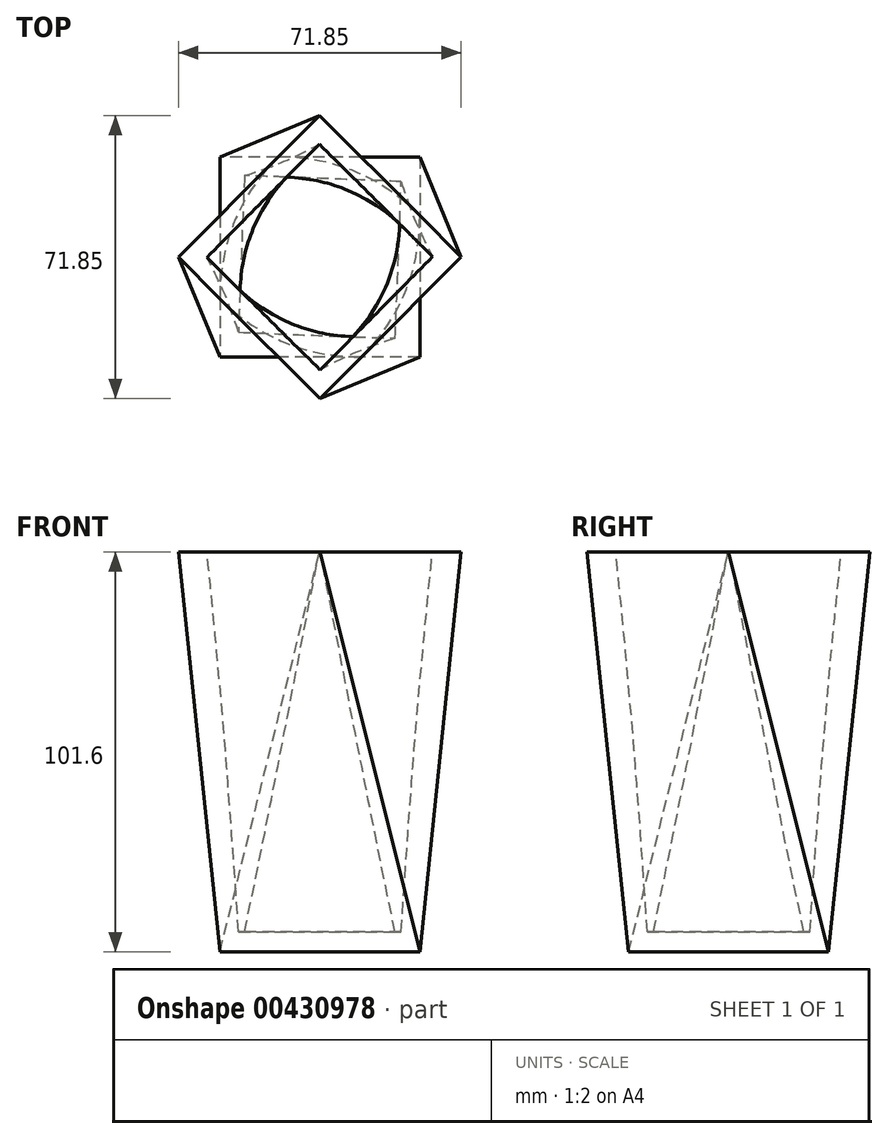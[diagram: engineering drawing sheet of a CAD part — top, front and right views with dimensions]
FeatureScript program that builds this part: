
annotation { "Feature Type Name" : "Feature", "Feature Type Description" : "" }
export const myFeature = defineFeature(function(context is Context, id is Id, definition is map)
    precondition{}
    {
        {
            var Q0;
            Q0=qCreatedBy(makeId("Top.planeOp"),FACE);
            var sketch = newSketch(context, id + "F0", { "sketchPlane" : qUnion([Q0])});
            skLineSegment(sketch, "E0.bottom", {"start": v(25.4, 25.4) * mm, "end": v(-25.4, 25.4) * mm});
            skLineSegment(sketch, "E0.top", {"start": v(25.4, -25.4) * mm, "end": v(-25.4, -25.4) * mm});
            skLineSegment(sketch, "E0.left", {"start": v(25.4, 25.4) * mm, "end": v(25.4, -25.4) * mm});
            skLineSegment(sketch, "E0.right", {"start": v(-25.4, 25.4) * mm, "end": v(-25.4, -25.4) * mm});
            skPoint(sketch, "E0.middle", {"position": v(0, 0) * mm});
            skSolve(sketch);
        }
        {
            var Q0;
            Q0=qCreatedBy(makeId("Top.planeOp"),FACE);
            cPlane(context, id + "F1", {"entities" : qUnion([Q0]), "cplaneType" : CPlaneType.OFFSET, "offset" : 101.6 * mm, "width" : 152.4 * mm, "height" : 152.4 * mm});
        }
        {
            var Q0;
            Q0=qCreatedBy(id+"F1.planeOp",FACE);
            var sketch = newSketch(context, id + "F2", { "sketchPlane" : qUnion([Q0])});
            skPoint(sketch, "E1.middle", {"position": v(0, 0) * mm});
            skLineSegment(sketch, "E2", {"start": v(-35.96, -0.07) * mm, "end": v(-0.07, 35.89) * mm});
            skLineSegment(sketch, "E3", {"start": v(-0.07, 35.89) * mm, "end": v(35.89, 0) * mm});
            skLineSegment(sketch, "E4", {"start": v(35.89, 0) * mm, "end": v(0, -35.96) * mm});
            skLineSegment(sketch, "E5", {"start": v(0, -35.96) * mm, "end": v(-35.96, -0.07) * mm});
            skSolve(sketch);
        }
        {
            var Q0;
            Q0=makeQuery(id+"F0.imprint","IMPRINT",FACE,{"disambiguationData":[TD([[makeQuery(id+"F0.imprint","IMPRINT",EDGE,{"derivedFrom":sQuery(id+"F0.wireOp",EDGE,"E0.bottom")}),1.0]])]});
            var Q1;
            Q1=makeQuery(id+"F2.imprint","IMPRINT",FACE,{"disambiguationData":[TD([[makeQuery(id+"F2.imprint","IMPRINT",EDGE,{"derivedFrom":sQuery(id+"F2.wireOp",EDGE,"E2")}),-1.0]])]});
            loft(context, id + "F3", {"sheetProfilesArray" : [{ "sheetProfileEntities" : qUnion([Q0]) }, { "sheetProfileEntities" : qUnion([Q1]) }]});
        }
        {
            var Q0;
            Q0=makeQuery(id+"F3.opLoft","CAP_FACE",FACE,{"disambiguationData":[OSD([makeQuery(id+"F2.imprint","IMPRINT",FACE,{"disambiguationData":[TD([[makeQuery(id+"F2.imprint","IMPRINT",EDGE,{"derivedFrom":sQuery(id+"F2.wireOp",EDGE,"E2")}),-1.0]])]})])],"isStart":true});
            shell(context, id + "F4", {"entities" : qUnion([Q0]), "thickness" : 5.08 * mm});
        }
    });
